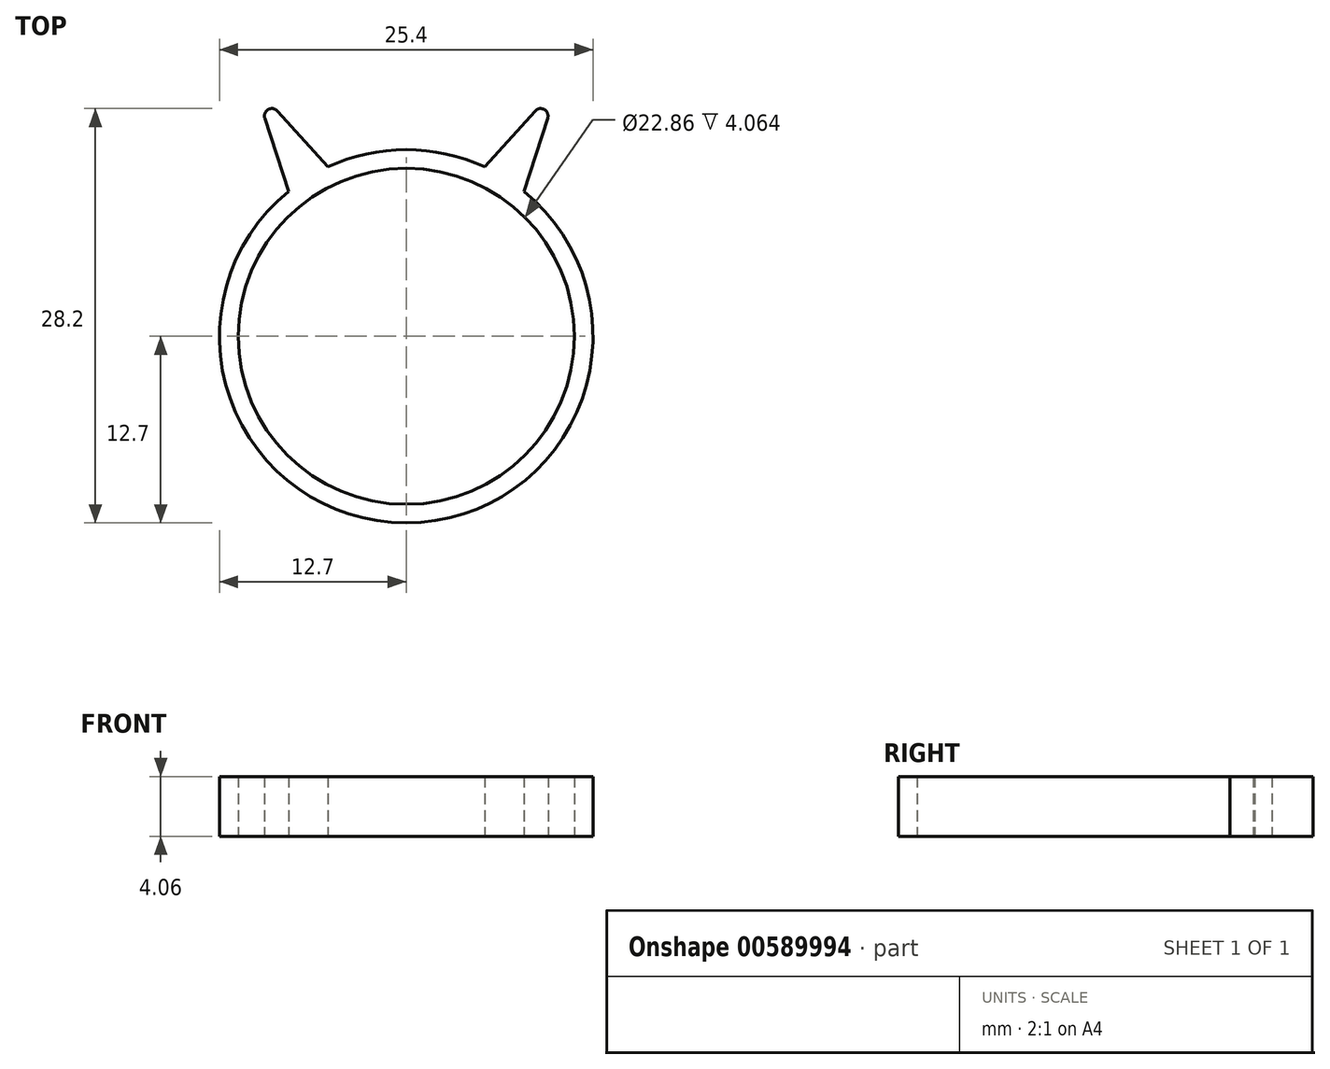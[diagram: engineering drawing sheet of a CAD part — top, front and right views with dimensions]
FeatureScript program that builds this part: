
annotation { "Feature Type Name" : "Feature", "Feature Type Description" : "" }
export const myFeature = defineFeature(function(context is Context, id is Id, definition is map)
    precondition{}
    {
        {
            var Q0;
            Q0=qCreatedBy(makeId("Top.planeOp"),FACE);
            var sketch = newSketch(context, id + "F0", { "sketchPlane" : qUnion([Q0])});
            skCircle(sketch, "E0", {"center": v(0, 0) * mm, "radius": 12.7 * mm});
            skLineSegment(sketch, "E1", {"start": v(-8, 9.86) * mm, "end": v(-10.36, 17.1) * mm});
            skLineSegment(sketch, "E2", {"start": v(-10.36, 17.1) * mm, "end": v(-5.33, 11.53) * mm});
            skLineSegment(sketch, "E3", {"start": v(0, 0) * mm, "end": v(0, 12.7) * mm, "construction": true});
            skLineSegment(sketch, "E4.MirrorCS", {"start": v(8, 9.86) * mm, "end": v(10.36, 17.1) * mm});
            skLineSegment(sketch, "E5.MirrorCS", {"start": v(10.36, 17.1) * mm, "end": v(5.33, 11.53) * mm});
            skCircle(sketch, "E6", {"center": v(0, 0) * mm, "radius": 11.43 * mm});
            skSolve(sketch);
        }
        {
            var Q0;
            Q0 = qSketchRegion(id + "F0", true);
            extrude(context, id + "F1", {"entities" : qUnion([Q0]), "depth" : 4.06 * mm, "offsetDistance" : 25.4 * mm});
        }
        {
            var Q0;
            Q0=makeQuery(id+"F1.opExtrude","SWEPT_EDGE",EDGE,{"disambiguationData":[OSD([sQuery(id+"F0.wireOp",EDGE,"E4.MirrorCS"),sQuery(id+"F0.wireOp",EDGE,"E5.MirrorCS")])]});
            var Q1;
            Q1=makeQuery(id+"F1.opExtrude","SWEPT_EDGE",EDGE,{"disambiguationData":[OSD([sQuery(id+"F0.wireOp",EDGE,"E1"),sQuery(id+"F0.wireOp",EDGE,"E2")])]});
            fillet(context, id + "F2", {"entities" : qUnion([Q0, Q1]), "radius" : 0.5 * mm, "tangentPropagation" : true, "allowEdgeOverflow" : false});
        }
    });
